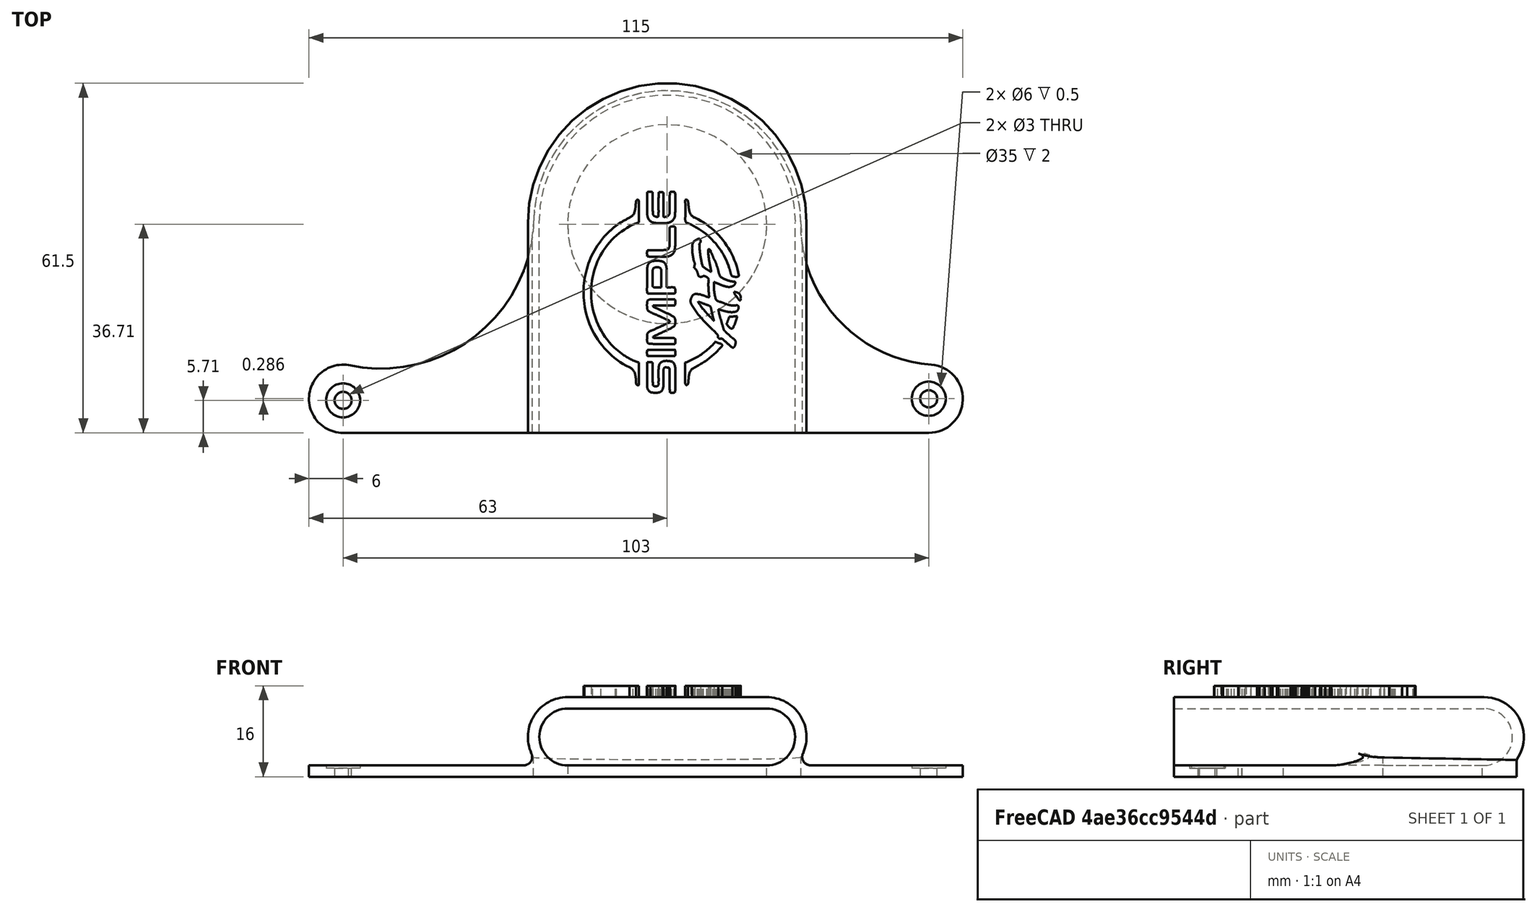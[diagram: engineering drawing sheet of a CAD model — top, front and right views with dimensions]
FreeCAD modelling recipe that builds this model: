
FCSTD DOCUMENT  (FreeCAD 1.1R44555 (Git))
Label: Ender3FanCoverSimpleAF
License: All rights reserved
LicenseURL: https://en.wikipedia.org/wiki/All_rights_reserved
objects: Part::Feature×1, App::Point×1, PartDesign::FeatureBase×1, Sketcher::SketchObject×1, PartDesign::Pad×1, PartDesign::Body×1
note: 9 computed .brp shape members not serialized (recipe doc carries the construction recipe); baked Part::Feature solids carry a one-line shape summary decoded from their .brp

FEATURE [Part::Feature] Part__Feature  label="Ender 3 fan redirect v4"
  shape: bbox 115 x 63.52 x 14 mm, 30 faces (baked)
FEATURE [App::Point] Origin001
  Role = Origin
FEATURE [PartDesign::FeatureBase] BaseFeature
  BaseFeature = -> Part__Feature
  Suppressed = false
FEATURE [Sketcher::SketchObject] Sketch004
  ArcFitTolerance = 1e-06
  AttachmentOffset = pos=(42,37,0) rot=(0,0,1;0rad)
  AttachmentSupport = -> [BaseFeature]
  ExternalTypes = [0]
  FullyConstrained = false
  MakeInternals = false
  MapMode = 5
  Placement = pos=(42,37,14) rot=(0,0,1;0rad)
  sketch-geometry (160):
    g0: BSplineCurve PolesCount=4 KnotsCount=2 Degree=3 IsPeriodic=0
    g1: BSplineCurve PolesCount=4 KnotsCount=2 Degree=3 IsPeriodic=0
    g2: BSplineCurve PolesCount=4 KnotsCount=2 Degree=3 IsPeriodic=0
    g3: BSplineCurve PolesCount=4 KnotsCount=2 Degree=3 IsPeriodic=0
    g4: BSplineCurve PolesCount=4 KnotsCount=2 Degree=3 IsPeriodic=0
    g5: BSplineCurve PolesCount=4 KnotsCount=2 Degree=3 IsPeriodic=0
    g6: BSplineCurve PolesCount=4 KnotsCount=2 Degree=3 IsPeriodic=0
    g7: BSplineCurve PolesCount=4 KnotsCount=2 Degree=3 IsPeriodic=0
    g8: BSplineCurve PolesCount=4 KnotsCount=2 Degree=3 IsPeriodic=0
    g9: BSplineCurve PolesCount=4 KnotsCount=2 Degree=3 IsPeriodic=0
    g10: BSplineCurve PolesCount=4 KnotsCount=2 Degree=3 IsPeriodic=0
    g11: BSplineCurve PolesCount=4 KnotsCount=2 Degree=3 IsPeriodic=0
    g12: BSplineCurve PolesCount=4 KnotsCount=2 Degree=3 IsPeriodic=0
    g13: BSplineCurve PolesCount=4 KnotsCount=2 Degree=3 IsPeriodic=0
    g14: BSplineCurve PolesCount=4 KnotsCount=2 Degree=3 IsPeriodic=0
    g15: BSplineCurve PolesCount=4 KnotsCount=2 Degree=3 IsPeriodic=0
    g16: BSplineCurve PolesCount=4 KnotsCount=2 Degree=3 IsPeriodic=0
    g17: BSplineCurve PolesCount=4 KnotsCount=2 Degree=3 IsPeriodic=0
    g18: BSplineCurve PolesCount=4 KnotsCount=2 Degree=3 IsPeriodic=0
    g19: BSplineCurve PolesCount=4 KnotsCount=2 Degree=3 IsPeriodic=0
    g20: BSplineCurve PolesCount=4 KnotsCount=2 Degree=3 IsPeriodic=0
    g21: BSplineCurve PolesCount=4 KnotsCount=2 Degree=3 IsPeriodic=0
    g22: BSplineCurve PolesCount=4 KnotsCount=2 Degree=3 IsPeriodic=0
    g23: BSplineCurve PolesCount=4 KnotsCount=2 Degree=3 IsPeriodic=0
    g24: BSplineCurve PolesCount=4 KnotsCount=2 Degree=3 IsPeriodic=0
    g25: BSplineCurve PolesCount=4 KnotsCount=2 Degree=3 IsPeriodic=0
    g26: BSplineCurve PolesCount=4 KnotsCount=2 Degree=3 IsPeriodic=0
    g27: BSplineCurve PolesCount=4 KnotsCount=2 Degree=3 IsPeriodic=0
    g28: BSplineCurve PolesCount=4 KnotsCount=2 Degree=3 IsPeriodic=0
    g29: BSplineCurve PolesCount=4 KnotsCount=2 Degree=3 IsPeriodic=0
    g30: BSplineCurve PolesCount=4 KnotsCount=2 Degree=3 IsPeriodic=0
    g31: BSplineCurve PolesCount=4 KnotsCount=2 Degree=3 IsPeriodic=0
    g32: BSplineCurve PolesCount=4 KnotsCount=2 Degree=3 IsPeriodic=0
    g33: BSplineCurve PolesCount=4 KnotsCount=2 Degree=3 IsPeriodic=0
    g34: BSplineCurve PolesCount=4 KnotsCount=2 Degree=3 IsPeriodic=0
    g35: BSplineCurve PolesCount=4 KnotsCount=2 Degree=3 IsPeriodic=0
    g36: BSplineCurve PolesCount=4 KnotsCount=2 Degree=3 IsPeriodic=0
    g37: BSplineCurve PolesCount=4 KnotsCount=2 Degree=3 IsPeriodic=0
    g38: BSplineCurve PolesCount=4 KnotsCount=2 Degree=3 IsPeriodic=0
    g39: BSplineCurve PolesCount=4 KnotsCount=2 Degree=3 IsPeriodic=0
    g40: BSplineCurve PolesCount=4 KnotsCount=2 Degree=3 IsPeriodic=0
    g41: BSplineCurve PolesCount=4 KnotsCount=2 Degree=3 IsPeriodic=0
    g42: BSplineCurve PolesCount=4 KnotsCount=2 Degree=3 IsPeriodic=0
    g43: BSplineCurve PolesCount=4 KnotsCount=2 Degree=3 IsPeriodic=0
    g44: BSplineCurve PolesCount=4 KnotsCount=2 Degree=3 IsPeriodic=0
    g45: BSplineCurve PolesCount=4 KnotsCount=2 Degree=3 IsPeriodic=0
    g46: BSplineCurve PolesCount=4 KnotsCount=2 Degree=3 IsPeriodic=0
    g47: BSplineCurve PolesCount=4 KnotsCount=2 Degree=3 IsPeriodic=0
    g48: BSplineCurve PolesCount=4 KnotsCount=2 Degree=3 IsPeriodic=0
    g49: BSplineCurve PolesCount=4 KnotsCount=2 Degree=3 IsPeriodic=0
    g50: BSplineCurve PolesCount=4 KnotsCount=2 Degree=3 IsPeriodic=0
    g51: BSplineCurve PolesCount=4 KnotsCount=2 Degree=3 IsPeriodic=0
    g52: BSplineCurve PolesCount=4 KnotsCount=2 Degree=3 IsPeriodic=0
    g53: BSplineCurve PolesCount=4 KnotsCount=2 Degree=3 IsPeriodic=0
    g54: BSplineCurve PolesCount=4 KnotsCount=2 Degree=3 IsPeriodic=0
    g55: BSplineCurve PolesCount=4 KnotsCount=2 Degree=3 IsPeriodic=0
    g56: BSplineCurve PolesCount=4 KnotsCount=2 Degree=3 IsPeriodic=0
    g57: BSplineCurve PolesCount=4 KnotsCount=2 Degree=3 IsPeriodic=0
    g58: BSplineCurve PolesCount=4 KnotsCount=2 Degree=3 IsPeriodic=0
    g59: BSplineCurve PolesCount=4 KnotsCount=2 Degree=3 IsPeriodic=0
    g60: BSplineCurve PolesCount=4 KnotsCount=2 Degree=3 IsPeriodic=0
    g61: BSplineCurve PolesCount=4 KnotsCount=2 Degree=3 IsPeriodic=0
    g62: BSplineCurve PolesCount=4 KnotsCount=2 Degree=3 IsPeriodic=0
    g63: BSplineCurve PolesCount=4 KnotsCount=2 Degree=3 IsPeriodic=0
    g64: BSplineCurve PolesCount=4 KnotsCount=2 Degree=3 IsPeriodic=0
    g65: BSplineCurve PolesCount=4 KnotsCount=2 Degree=3 IsPeriodic=0
    g66: BSplineCurve PolesCount=4 KnotsCount=2 Degree=3 IsPeriodic=0
    g67: BSplineCurve PolesCount=4 KnotsCount=2 Degree=3 IsPeriodic=0
    g68: BSplineCurve PolesCount=4 KnotsCount=2 Degree=3 IsPeriodic=0
    g69: BSplineCurve PolesCount=4 KnotsCount=2 Degree=3 IsPeriodic=0
    g70: BSplineCurve PolesCount=4 KnotsCount=2 Degree=3 IsPeriodic=0
    g71: BSplineCurve PolesCount=4 KnotsCount=2 Degree=3 IsPeriodic=0
    g72: BSplineCurve PolesCount=4 KnotsCount=2 Degree=3 IsPeriodic=0
    g73: BSplineCurve PolesCount=4 KnotsCount=2 Degree=3 IsPeriodic=0
    g74: BSplineCurve PolesCount=4 KnotsCount=2 Degree=3 IsPeriodic=0
    g75: BSplineCurve PolesCount=4 KnotsCount=2 Degree=3 IsPeriodic=0
    g76: BSplineCurve PolesCount=4 KnotsCount=2 Degree=3 IsPeriodic=0
    g77: BSplineCurve PolesCount=4 KnotsCount=2 Degree=3 IsPeriodic=0
    g78: BSplineCurve PolesCount=4 KnotsCount=2 Degree=3 IsPeriodic=0
    g79: BSplineCurve PolesCount=4 KnotsCount=2 Degree=3 IsPeriodic=0
    g80: BSplineCurve PolesCount=4 KnotsCount=2 Degree=3 IsPeriodic=0
    g81: BSplineCurve PolesCount=4 KnotsCount=2 Degree=3 IsPeriodic=0
    g82: BSplineCurve PolesCount=4 KnotsCount=2 Degree=3 IsPeriodic=0
    g83: BSplineCurve PolesCount=4 KnotsCount=2 Degree=3 IsPeriodic=0
    g84: BSplineCurve PolesCount=4 KnotsCount=2 Degree=3 IsPeriodic=0
    g85: BSplineCurve PolesCount=4 KnotsCount=2 Degree=3 IsPeriodic=0
    g86: BSplineCurve PolesCount=4 KnotsCount=2 Degree=3 IsPeriodic=0
    g87: BSplineCurve PolesCount=4 KnotsCount=2 Degree=3 IsPeriodic=0
    g88: BSplineCurve PolesCount=4 KnotsCount=2 Degree=3 IsPeriodic=0
    g89: BSplineCurve PolesCount=4 KnotsCount=2 Degree=3 IsPeriodic=0
    g90: BSplineCurve PolesCount=4 KnotsCount=2 Degree=3 IsPeriodic=0
    g91: BSplineCurve PolesCount=4 KnotsCount=2 Degree=3 IsPeriodic=0
    g92: BSplineCurve PolesCount=4 KnotsCount=2 Degree=3 IsPeriodic=0
    g93: BSplineCurve PolesCount=4 KnotsCount=2 Degree=3 IsPeriodic=0
    g94: BSplineCurve PolesCount=4 KnotsCount=2 Degree=3 IsPeriodic=0
    g95: BSplineCurve PolesCount=4 KnotsCount=2 Degree=3 IsPeriodic=0
    g96: BSplineCurve PolesCount=4 KnotsCount=2 Degree=3 IsPeriodic=0
    g97: BSplineCurve PolesCount=4 KnotsCount=2 Degree=3 IsPeriodic=0
    g98: BSplineCurve PolesCount=4 KnotsCount=2 Degree=3 IsPeriodic=0
    g99: BSplineCurve PolesCount=4 KnotsCount=2 Degree=3 IsPeriodic=0
    g100: BSplineCurve PolesCount=4 KnotsCount=2 Degree=3 IsPeriodic=0
    g101: BSplineCurve PolesCount=4 KnotsCount=2 Degree=3 IsPeriodic=0
    g102: BSplineCurve PolesCount=4 KnotsCount=2 Degree=3 IsPeriodic=0
    g103: BSplineCurve PolesCount=4 KnotsCount=2 Degree=3 IsPeriodic=0
    g104: BSplineCurve PolesCount=4 KnotsCount=2 Degree=3 IsPeriodic=0
    g105: BSplineCurve PolesCount=2 KnotsCount=2 Degree=1 IsPeriodic=0
    g106: BSplineCurve PolesCount=4 KnotsCount=2 Degree=3 IsPeriodic=0
    g107: BSplineCurve PolesCount=4 KnotsCount=2 Degree=3 IsPeriodic=0
    g108: BSplineCurve PolesCount=4 KnotsCount=2 Degree=3 IsPeriodic=0
    g109: BSplineCurve PolesCount=4 KnotsCount=2 Degree=3 IsPeriodic=0
    g110: BSplineCurve PolesCount=4 KnotsCount=2 Degree=3 IsPeriodic=0
    g111: BSplineCurve PolesCount=4 KnotsCount=2 Degree=3 IsPeriodic=0
    g112: BSplineCurve PolesCount=4 KnotsCount=2 Degree=3 IsPeriodic=0
    g113: BSplineCurve PolesCount=4 KnotsCount=2 Degree=3 IsPeriodic=0
    g114: BSplineCurve PolesCount=4 KnotsCount=2 Degree=3 IsPeriodic=0
    g115: BSplineCurve PolesCount=4 KnotsCount=2 Degree=3 IsPeriodic=0
    g116: BSplineCurve PolesCount=4 KnotsCount=2 Degree=3 IsPeriodic=0
    g117: BSplineCurve PolesCount=4 KnotsCount=2 Degree=3 IsPeriodic=0
    g118: BSplineCurve PolesCount=4 KnotsCount=2 Degree=3 IsPeriodic=0
    g119: BSplineCurve PolesCount=4 KnotsCount=2 Degree=3 IsPeriodic=0
    g120: BSplineCurve PolesCount=4 KnotsCount=2 Degree=3 IsPeriodic=0
    g121: BSplineCurve PolesCount=4 KnotsCount=2 Degree=3 IsPeriodic=0
    g122: BSplineCurve PolesCount=4 KnotsCount=2 Degree=3 IsPeriodic=0
    g123: BSplineCurve PolesCount=4 KnotsCount=2 Degree=3 IsPeriodic=0
    g124: BSplineCurve PolesCount=4 KnotsCount=2 Degree=3 IsPeriodic=0
    g125: BSplineCurve PolesCount=4 KnotsCount=2 Degree=3 IsPeriodic=0
    g126: BSplineCurve PolesCount=4 KnotsCount=2 Degree=3 IsPeriodic=0
    g127: BSplineCurve PolesCount=4 KnotsCount=2 Degree=3 IsPeriodic=0
    g128: BSplineCurve PolesCount=4 KnotsCount=2 Degree=3 IsPeriodic=0
    g129: BSplineCurve PolesCount=4 KnotsCount=2 Degree=3 IsPeriodic=0
    g130: BSplineCurve PolesCount=4 KnotsCount=2 Degree=3 IsPeriodic=0
    g131: BSplineCurve PolesCount=4 KnotsCount=2 Degree=3 IsPeriodic=0
    g132: BSplineCurve PolesCount=4 KnotsCount=2 Degree=3 IsPeriodic=0
    g133: BSplineCurve PolesCount=4 KnotsCount=2 Degree=3 IsPeriodic=0
    g134: BSplineCurve PolesCount=4 KnotsCount=2 Degree=3 IsPeriodic=0
    g135: BSplineCurve PolesCount=4 KnotsCount=2 Degree=3 IsPeriodic=0
    g136: BSplineCurve PolesCount=4 KnotsCount=2 Degree=3 IsPeriodic=0
    g137: BSplineCurve PolesCount=4 KnotsCount=2 Degree=3 IsPeriodic=0
    g138: BSplineCurve PolesCount=4 KnotsCount=2 Degree=3 IsPeriodic=0
    g139: BSplineCurve PolesCount=4 KnotsCount=2 Degree=3 IsPeriodic=0
    g140: BSplineCurve PolesCount=4 KnotsCount=2 Degree=3 IsPeriodic=0
    g141: BSplineCurve PolesCount=4 KnotsCount=2 Degree=3 IsPeriodic=0
    g142: BSplineCurve PolesCount=4 KnotsCount=2 Degree=3 IsPeriodic=0
    g143: BSplineCurve PolesCount=4 KnotsCount=2 Degree=3 IsPeriodic=0
    g144: BSplineCurve PolesCount=4 KnotsCount=2 Degree=3 IsPeriodic=0
    g145: BSplineCurve PolesCount=4 KnotsCount=2 Degree=3 IsPeriodic=0
    g146: BSplineCurve PolesCount=4 KnotsCount=2 Degree=3 IsPeriodic=0
    g147: BSplineCurve PolesCount=4 KnotsCount=2 Degree=3 IsPeriodic=0
    g148: BSplineCurve PolesCount=4 KnotsCount=2 Degree=3 IsPeriodic=0
    g149: BSplineCurve PolesCount=4 KnotsCount=2 Degree=3 IsPeriodic=0
    g150: BSplineCurve PolesCount=4 KnotsCount=2 Degree=3 IsPeriodic=0
    g151: BSplineCurve PolesCount=4 KnotsCount=2 Degree=3 IsPeriodic=0
    g152: BSplineCurve PolesCount=4 KnotsCount=2 Degree=3 IsPeriodic=0
    g153: BSplineCurve PolesCount=4 KnotsCount=2 Degree=3 IsPeriodic=0
    g154: BSplineCurve PolesCount=4 KnotsCount=2 Degree=3 IsPeriodic=0
    g155: BSplineCurve PolesCount=4 KnotsCount=2 Degree=3 IsPeriodic=0
    g156: BSplineCurve PolesCount=4 KnotsCount=2 Degree=3 IsPeriodic=0
    g157: BSplineCurve PolesCount=4 KnotsCount=2 Degree=3 IsPeriodic=0
    g158: BSplineCurve PolesCount=4 KnotsCount=2 Degree=3 IsPeriodic=0
    g159: BSplineCurve PolesCount=4 KnotsCount=2 Degree=3 IsPeriodic=0
  constraints (160):
    c: Coincident(g10,g11)
    c: Coincident(g4,g5)
    c: Coincident(g11,g12)
    c: Coincident(g0,g12)
    c: Coincident(g5,g6)
    c: Coincident(g9,g10)
    c: Coincident(g0,g1)
    c: Coincident(g8,g9)
    c: Coincident(g1,g2)
    c: Coincident(g3,g4)
    c: Coincident(g2,g3)
    c: Coincident(g7,g8)
    c: Coincident(g6,g7)
    c: Coincident(g79,g80)
    c: Coincident(g96,g97)
    c: Coincident(g109,g110)
    c: Coincident(g13,g26)
    c: Coincident(g110,g111)
    c: Coincident(g13,g14)
    c: Coincident(g136,g137)
    c: Coincident(g102,g103)
    c: Coincident(g82,g83)
    c: Coincident(g137,g138)
    c: Coincident(g103,g104)
    c: Coincident(g78,g79)
    c: Coincident(g83,g84)
    c: Coincident(g80,g81)
    c: Coincident(g25,g26)
    c: Coincident(g95,g96)
    c: Coincident(g108,g109)
    c: Coincident(g73,g81)
    c: Coincident(g14,g15)
    c: Coincident(g111,g112)
    c: Coincident(g127,g131)
    c: Coincident(g127,g128)
    c: Coincident(g87,g88)
    c: Coincident(g91,g92)
    c: Coincident(g112,g113)
    c: Coincident(g15,g16)
    c: Coincident(g130,g131)
    c: Coincident(g97,g98)
    c: Coincident(g88,g89)
    c: Coincident(g84,g85)
    c: Coincident(g92,g93)
    c: Coincident(g113,g114)
    c: Coincident(g16,g17)
    c: Coincident(g17,g18)
    c: Coincident(g114,g115)
    c: Coincident(g82,g100)
    c: Coincident(g129,g130)
    c: Coincident(g128,g129)
    c: Coincident(g73,g74)
    c: Coincident(g107,g108)
    c: Coincident(g135,g136)
    c: Coincident(g18,g19)
    c: Coincident(g19,g20)
    c: Coincident(g106,g107)
    c: Coincident(g24,g25)
    c: Coincident(g99,g100)
    c: Coincident(g106,g120)
    c: Coincident(g74,g75)
    c: Coincident(g75,g76)
    c: Coincident(g138,g139)
    c: Coincident(g119,g120)
    c: Coincident(g139,g140)
    c: Coincident(g132,g140)
    c: Coincident(g20,g21)
    c: Coincident(g98,g99)
    c: Coincident(g118,g119)
    c: Coincident(g132,g133)
    c: Coincident(g21,g22)
    c: Coincident(g115,g116)
    c: Coincident(g90,g91)
    c: Coincident(g89,g90)
    c: Coincident(g77,g78)
    c: Coincident(g134,g135)
    c: Coincident(g85,g86)
    c: Coincident(g86,g87)
    c: Coincident(g23,g24)
    c: Coincident(g104,g105)
    c: Coincident(g101,g102)
    c: Coincident(g94,g95)
    c: Coincident(g117,g118)
    c: Coincident(g101,g105)
    c: Coincident(g22,g23)
    c: Coincident(g93,g94)
    c: Coincident(g76,g77)
    c: Coincident(g133,g134)
    c: Coincident(g116,g117)
    c: Coincident(g148,g149)
    c: Coincident(g157,g158)
    c: Coincident(g158,g159)
    c: Coincident(g147,g148)
    c: Coincident(g146,g147)
    c: Coincident(g156,g157)
    c: Coincident(g149,g150)
    c: Coincident(g57,g58)
    c: Coincident(g155,g156)
    c: Coincident(g46,g47)
    c: Coincident(g56,g57)
    c: Coincident(g47,g48)
    c: Coincident(g48,g49)
    c: Coincident(g45,g46)
    c: Coincident(g150,g151)
    c: Coincident(g55,g56)
    c: Coincident(g49,g50)
    c: Coincident(g122,g123)
    c: Coincident(g43,g44)
    c: Coincident(g44,g45)
    c: Coincident(g54,g55)
    c: Coincident(g123,g124)
    c: Coincident(g42,g43)
    c: Coincident(g50,g51)
    c: Coincident(g124,g125)
    c: Coincident(g53,g54)
    c: Coincident(g40,g41)
    c: Coincident(g52,g53)
    c: Coincident(g51,g52)
    c: Coincident(g58,g59)
    c: Coincident(g121,g122)
    c: Coincident(g39,g40)
    c: Coincident(g41,g42)
    c: Coincident(g38,g39)
    c: Coincident(g125,g126)
    c: Coincident(g121,g126)
    c: Coincident(g32,g33)
    c: Coincident(g31,g32)
    c: Coincident(g153,g159)
    c: Coincident(g37,g38)
    c: Coincident(g59,g60)
    c: Coincident(g67,g68)
    c: Coincident(g154,g155)
    c: Coincident(g66,g67)
    c: Coincident(g36,g37)
    c: Coincident(g60,g61)
    c: Coincident(g153,g154)
    c: Coincident(g65,g66)
    c: Coincident(g68,g69)
    c: Coincident(g71,g72)
    c: Coincident(g141,g144)
    c: Coincident(g33,g34)
    c: Coincident(g64,g65)
    c: Coincident(g145,g146)
    c: Coincident(g141,g142)
    c: Coincident(g63,g64)
    c: Coincident(g145,g152)
    c: Coincident(g143,g144)
    c: Coincident(g61,g62)
    c: Coincident(g34,g35)
    c: Coincident(g29,g30)
    c: Coincident(g35,g36)
    c: Coincident(g62,g63)
    c: Coincident(g27,g30)
    c: Coincident(g69,g70)
    c: Coincident(g70,g71)
    c: Coincident(g142,g143)
    c: Coincident(g28,g29)
    c: Coincident(g151,g152)
    c: Coincident(g27,g28)
    c: Coincident(g31,g72)
FEATURE [PartDesign::Pad] Pad
  BaseFeature = -> BaseFeature
  Direction = (0,0,1)
  Length = 2
  Length2 = 10
  Profile = -> Sketch004
  ReferenceAxis = -> Sketch004 [N_Axis]
  Refine = true
  SideType = 0
  Suppressed = false
  Type = 0
  Type2 = 0
FEATURE [PartDesign::Body] Body
  AllowCompound = true
  BaseFeature = -> Part__Feature
  Group = -> [BaseFeature,Sketch004,Pad]
  Origin = -> Origin
  Tip = -> Pad
